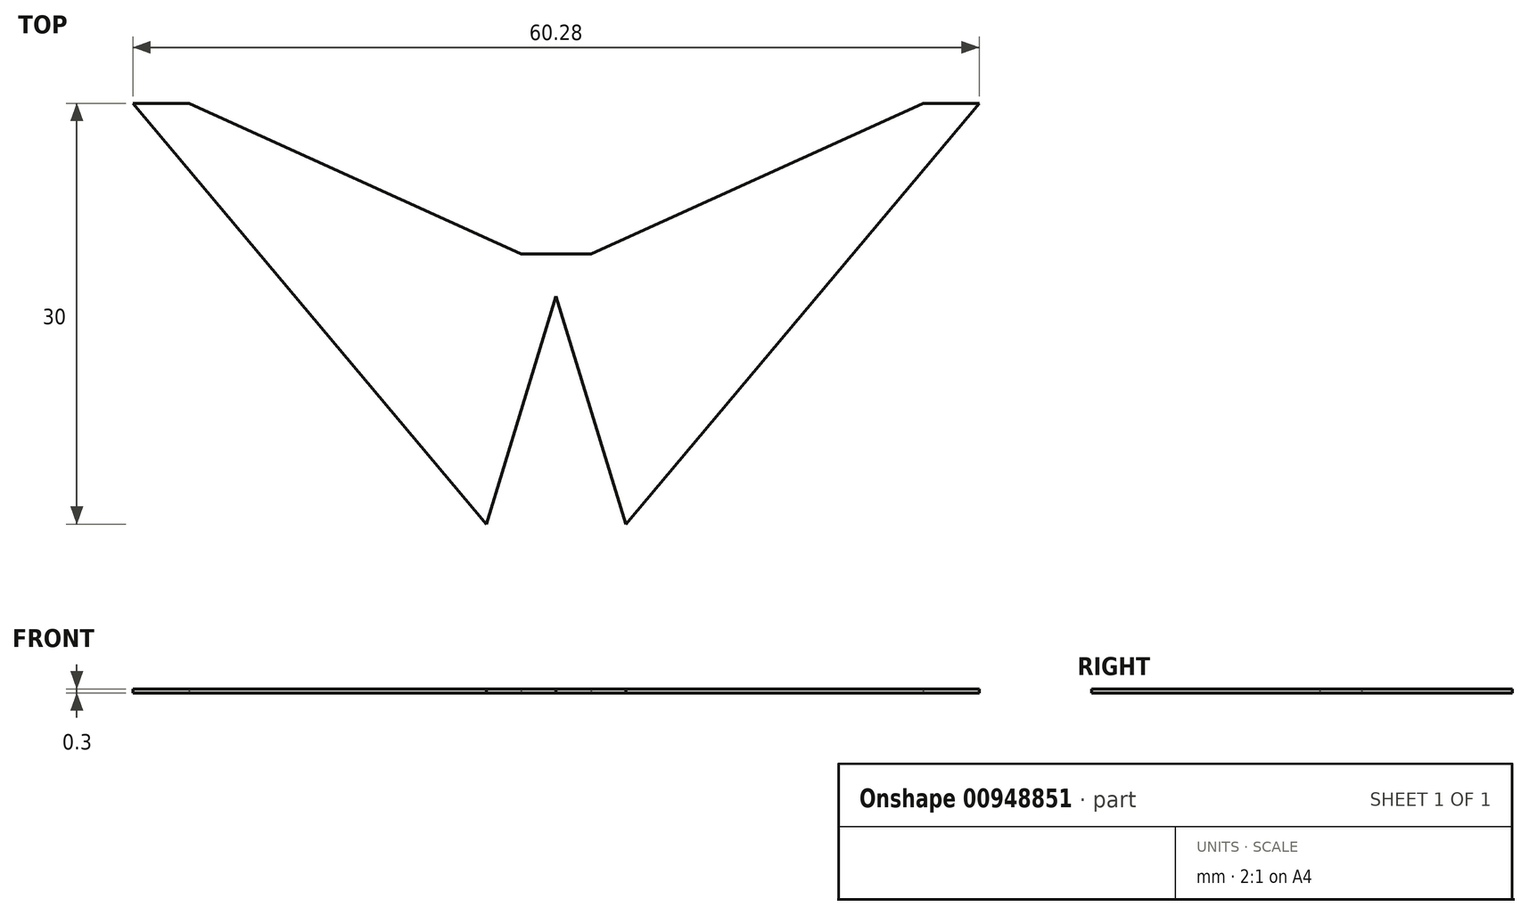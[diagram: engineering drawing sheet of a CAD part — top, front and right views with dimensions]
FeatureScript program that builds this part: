
annotation { "Feature Type Name" : "Feature", "Feature Type Description" : "" }
export const myFeature = defineFeature(function(context is Context, id is Id, definition is map)
    precondition{}
    {
        {
            var Q0;
            Q0=qCreatedBy(makeId("Top.planeOp"),FACE);
            var sketch = newSketch(context, id + "F0", { "sketchPlane" : qUnion([Q0])});
            skLineSegment(sketch, "E0", {"start": v(-4.97, 0.73) * mm, "end": v(-30.14, 30.73) * mm});
            skLineSegment(sketch, "E1", {"start": v(-30.14, 30.73) * mm, "end": v(-26.14, 30.73) * mm});
            skLineSegment(sketch, "E2", {"start": v(30.14, 30.73) * mm, "end": v(4.97, 0.73) * mm});
            skLineSegment(sketch, "E3", {"start": v(-4.97, 0.73) * mm, "end": v(0, 16.99) * mm});
            skLineSegment(sketch, "E4", {"start": v(0, 16.99) * mm, "end": v(4.97, 0.73) * mm});
            skLineSegment(sketch, "E5", {"start": v(-2.5, 19.99) * mm, "end": v(2.5, 19.99) * mm});
            skLineSegment(sketch, "E6", {"start": v(-2.5, 19.99) * mm, "end": v(-26.14, 30.73) * mm});
            skLineSegment(sketch, "E7", {"start": v(2.5, 19.99) * mm, "end": v(26.14, 30.73) * mm});
            skLineSegment(sketch, "E8.trimOffspring", {"start": v(26.14, 30.73) * mm, "end": v(30.14, 30.73) * mm});
            skSolve(sketch);
        }
        {
            var Q0;
            Q0 = qSketchRegion(id + "F0", true);
            extrude(context, id + "F1", {"entities" : qUnion([Q0]), "depth" : 0.3 * mm, "offsetDistance" : 25 * mm});
        }
    });
